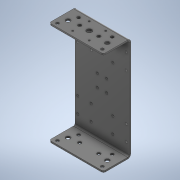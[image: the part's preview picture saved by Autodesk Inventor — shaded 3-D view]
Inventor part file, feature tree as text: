
AUTODESK INVENTOR PART (.ipt)
format: ipt  version: 2020 (Build 240168000, 168)  size: 270,848 bytes
history: native  units: mm
features: sketch x8, other x8, sheet_metal_op x4, fillet x1, pattern_linear x1
ambient origin geometry x8: Origin, YZ Plane, XZ Plane, XY Plane, X Axis, Y Axis, Z Axis, Center Point
bodies: Solid1 (feature_tree)
feature tree (22):
  sheet_metal_op  "Face1"
  sheet_metal_op  "Flange1"
  fillet  "Fillet1"  Radius=105.0mm
  pattern_linear  "Rectangular Pattern1"  Count1=20  [1 undecoded]
  sketch  "Sketch1"  dims[d2=3.0mm]
  other  "Plate1"
  sketch  "Sketch2"  dims[d3=3.0mm]
  other  "Plate2"
  sheet_metal_op  "Bend1"
  sheet_metal_op  "Corner1"
  sketch  "Sketch3"  dims[d4=1.5mm]
  sketch  "Sketch4"  dims[d5=6.0mm]
  sketch  "Sketch5"  dims[d6=3.0mm]
  sketch  "Sketch6"  dims[d7=53.0mm d8=90.0deg d9=3.0mm]
  sketch  "Sketch7"  dims[d10=12.0mm]
  sketch  "Sketch8"  dims[d11=3.0mm d12=3.0mm d13=8.3mm d14=8.3mm d15=76.0mm d16=38.0mm d17=22.0mm d18=22.0mm d19=3.0mm d20=0.0mm d21=37.0mm d22=18.5mm d23=6.5mm d24=6.5mm d25=25.0mm d26=25.0mm d27=3.0mm d28=0.0mm d29=4.0mm d30=32.0mm d31=32.0mm d32=0.0mm d33=25.0mm d34=3.5mm d35=3.5mm d36=3.5mm d37=3.5mm d38=10.0mm d39=3.0mm d40=0.0mm d41=6.5mm d42=6.5mm d43=25.0mm d44=25.0mm d45=37.0mm d46=18.5mm d47=30.5mm d48=26.0mm d49=4.5mm d50=4.5mm d51=4.5mm d52=4.5mm d53=60.0mm d54=34.0mm d55=3.0mm d56=0.0mm d57=20.0mm d59=68.0mm d60=20.0mm d62=120.0mm d63=24.0mm d64=18.0mm d65=4.5mm d66=4.5mm d67=4.5mm d68=4.5mm d69=3.0mm d70=0.0mm d71=16.0mm d72=12.217305mm d73=16.0mm d74=19.198622mm d75=6.0mm d76=6.0mm d77=16.0mm d78=19.198622mm d79=16.0mm d80=12.217305mm d81=6.0mm d82=6.0mm d83=3.0mm d84=0.0mm]
  other  "Cut1"
  other  "Cut2"
  other  "Cut3"
  other  "Cut4"
  other  "Cut5"
  other  "Cut6"
note: 1 required parameter value undecoded (feature->parameter linkage not recoverable at this tier; creation-order binding heuristic only, values carry confidence <= 0.55)
